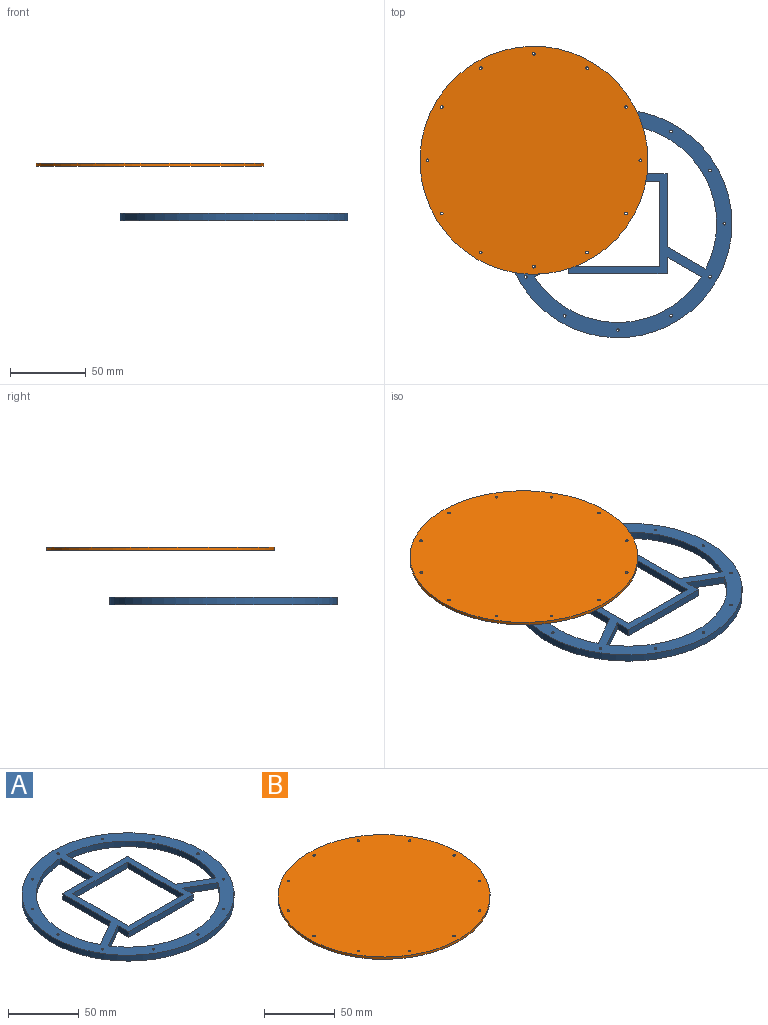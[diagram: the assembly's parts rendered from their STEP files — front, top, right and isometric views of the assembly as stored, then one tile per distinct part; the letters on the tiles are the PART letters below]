
ASSEMBLY  parts=2 mates=1
PART A: 35 faces, bbox 150x150x5 mm
  f0: cylinder r=0.88mm len=5mm, axis (0,0,1), area 27.5mm2, adj f32,f33
  f1: cylinder r=0.88mm len=5mm, axis (0,0,1), area 27.5mm2, adj f32,f33
  f2: cylinder r=0.88mm len=5mm, axis (0,0,1), area 27.5mm2, adj f32,f33
  f3: cylinder r=0.88mm len=5mm, axis (0,0,1), area 27.5mm2, adj f32,f33
  f4: cylinder r=0.88mm len=5mm, axis (0,0,1), area 27.5mm2, adj f32,f33
  f5: cylinder r=0.88mm len=5mm, axis (0,0,1), area 27.5mm2, adj f32,f33
  f6: cylinder r=0.88mm len=5mm, axis (0,0,1), area 27.5mm2, adj f32,f33
  f7: cylinder r=0.88mm len=5mm, axis (0,0,1), area 27.5mm2, adj f32,f33
  f8: cylinder r=0.88mm len=5mm, axis (0,0,1), area 27.5mm2, adj f32,f33
  f9: cylinder r=0.88mm len=5mm, axis (0,0,1), area 27.5mm2, adj f32,f33
  f10: cylinder r=0.88mm len=5mm, axis (0,0,1), area 27.5mm2, adj f32,f33
  f11: plane 56x5mm, normal (-1,0,0), area 280mm2, adj f12,f27,f32,f33
  f12: plane 54.67x5mm, normal (0,1,0), area 273.4mm2, adj f11,f13,f32,f33
  f13: plane 56x5mm, normal (1,0,0), area 280mm2, adj f12,f27,f32,f33
  f14: plane 25.4x14.66mm, normal (-0.5,0.87,0), area 146.6mm2, adj f15,f28,f32,f33
  f15: cylinder r=65mm len=94.8mm, axis (0,0,-1), area 650.7mm2, adj f14,f16,f32,f33
  f16: plane 31.93x5mm, normal (-1,0,0), area 159.7mm2, adj f15,f17,f32,f33
  f17: plane 29.34x5mm, normal (0,1,0), area 146.7mm2, adj f16,f28,f32,f33
  f18: cylinder r=65mm len=109.46mm, axis (0,0,-1), area 650.7mm2, adj f19,f29,f32,f33
  f19: plane 22.4x12.93mm, normal (0.5,-0.87,0), area 129.3mm2, adj f18,f20,f32,f33
  f20: plane 10.87x5mm, normal (-1,0,0), area 54.3mm2, adj f19,f21,f32,f33
  f21: plane 64.67x5mm, normal (0,-1,0), area 323.4mm2, adj f20,f22,f32,f33
  f22: plane 10.87x5mm, normal (1,0,0), area 54.3mm2, adj f21,f29,f32,f33
  f23: cylinder r=65mm len=94.8mm, axis (0,0,-1), area 650.7mm2, adj f24,f30,f32,f33
  f24: plane 25.4x14.66mm, normal (0.5,0.87,0), area 146.6mm2, adj f23,f25,f32,f33
  f25: plane 48.21x5mm, normal (1,0,0), area 241mm2, adj f24,f26,f32,f33
  f26: plane 29.34x5mm, normal (0,1,0), area 146.7mm2, adj f25,f30,f32,f33
  f27: plane 54.67x5mm, normal (0,-1,0), area 273.4mm2, adj f11,f13,f32,f33
  f28: plane 48.21x5mm, normal (-1,0,0), area 241mm2, adj f14,f17,f32,f33
  f29: plane 22.4x12.93mm, normal (-0.5,-0.87,0), area 129.3mm2, adj f18,f22,f32,f33
  f30: plane 31.93x5mm, normal (1,0,0), area 159.7mm2, adj f23,f26,f32,f33
  f31: cylinder r=75mm len=150mm, axis (0,0,-1), area 2356.2mm2, adj f32,f33
  f32: plane 150x150mm, normal (0,0,1), area 6099.6mm2, adj f0,f1,f2,f3,f4,f5,f6,f7
  f33: plane 150x150mm, normal (0,0,-1), area 6099.6mm2, adj f0,f1,f2,f3,f4,f5,f6,f7
  f34: cylinder r=0.88mm len=5mm, axis (0,0,1), area 27.5mm2, adj f32,f33
PART B: 15 faces, bbox 150x150x2 mm
  f0: cylinder r=0.88mm len=2mm, axis (0,0,1), area 11mm2, adj f12,f13
  f1: cylinder r=0.88mm len=2mm, axis (0,0,1), area 11mm2, adj f12,f13
  f2: cylinder r=0.88mm len=2mm, axis (0,0,1), area 11mm2, adj f12,f13
  f3: cylinder r=0.88mm len=2mm, axis (0,0,1), area 11mm2, adj f12,f13
  f4: cylinder r=0.88mm len=2mm, axis (0,0,1), area 11mm2, adj f12,f13
  f5: cylinder r=0.88mm len=2mm, axis (0,0,1), area 11mm2, adj f12,f13
  f6: cylinder r=0.88mm len=2mm, axis (0,0,1), area 11mm2, adj f12,f13
  f7: cylinder r=0.88mm len=2mm, axis (0,0,1), area 11mm2, adj f12,f13
  f8: cylinder r=0.88mm len=2mm, axis (0,0,1), area 11mm2, adj f12,f13
  f9: cylinder r=0.88mm len=2mm, axis (0,0,1), area 11mm2, adj f12,f13
  f10: cylinder r=0.88mm len=2mm, axis (0,0,1), area 11mm2, adj f12,f13
  f11: cylinder r=75mm len=150mm, axis (0,0,-1), area 942.5mm2, adj f12,f13
  f12: plane 150x150mm, normal (0,0,1), area 17642.6mm2, adj f0,f1,f2,f3,f4,f5,f6,f7
  f13: plane 150x150mm, normal (0,0,-1), area 17642.6mm2, adj f0,f1,f2,f3,f4,f5,f6,f7
  f14: cylinder r=0.88mm len=2mm, axis (0,0,1), area 11mm2, adj f12,f13
PLACE A t=(0.73,0.23,-2.78)mm
PLACE B t=(-54.53,41.9,33.21)mm
MATE parallel B.f4 <-> A.f32  axis (0,0,-1) through (-19.53,-18.72,33.21)mm
